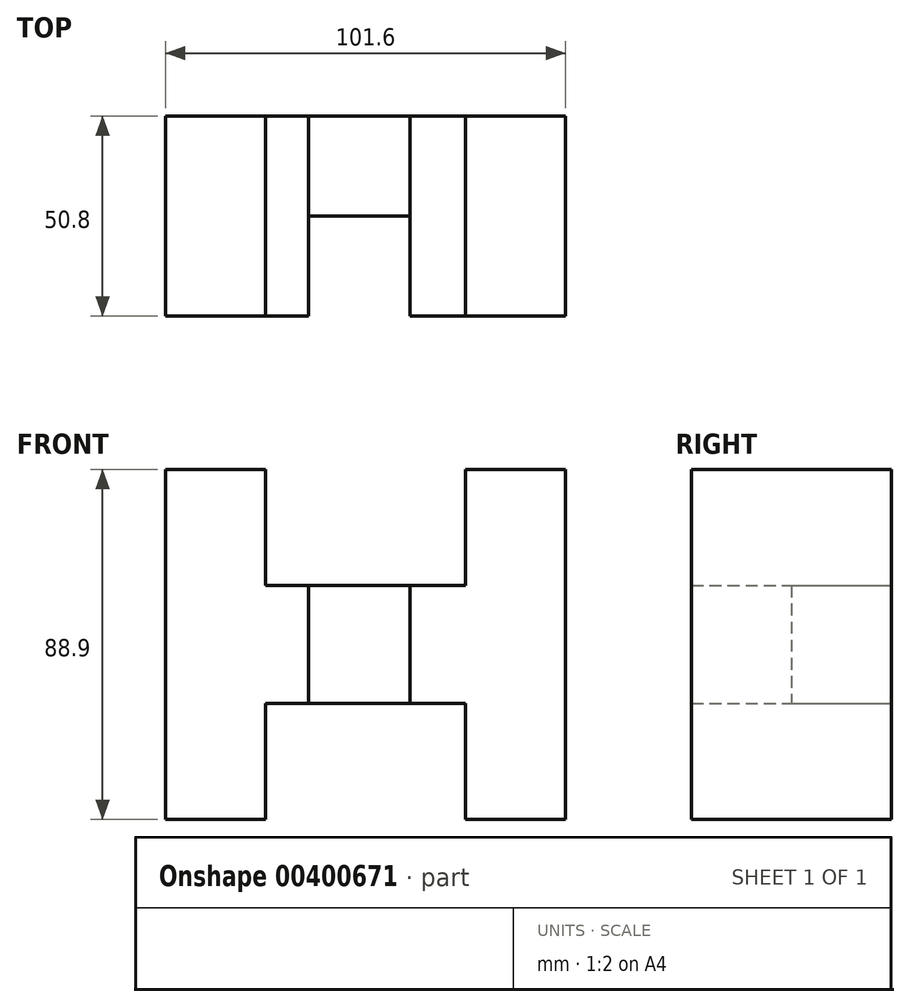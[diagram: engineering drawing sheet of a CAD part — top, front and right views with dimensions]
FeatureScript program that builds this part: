
annotation { "Feature Type Name" : "Feature", "Feature Type Description" : "" }
export const myFeature = defineFeature(function(context is Context, id is Id, definition is map)
    precondition{}
    {
        {
            var Q0;
            Q0=qCreatedBy(makeId("Front.planeOp"),FACE);
            var sketch = newSketch(context, id + "F0", { "sketchPlane" : qUnion([Q0])});
            skLineSegment(sketch, "E0", {"start": v(52.34, 49.99) * mm, "end": v(52.34, -38.91) * mm});
            skLineSegment(sketch, "E1", {"start": v(52.34, -38.91) * mm, "end": v(26.94, -38.91) * mm});
            skLineSegment(sketch, "E2", {"start": v(26.94, -38.91) * mm, "end": v(26.94, -9.45) * mm});
            skLineSegment(sketch, "E3", {"start": v(26.94, -9.45) * mm, "end": v(-23.86, -9.45) * mm});
            skLineSegment(sketch, "E4", {"start": v(-23.86, -9.45) * mm, "end": v(-23.86, -38.91) * mm});
            skLineSegment(sketch, "E5", {"start": v(-23.86, -38.91) * mm, "end": v(-49.26, -38.91) * mm});
            skLineSegment(sketch, "E6", {"start": v(-49.26, -38.91) * mm, "end": v(-49.26, 49.99) * mm});
            skLineSegment(sketch, "E7", {"start": v(-49.26, 49.99) * mm, "end": v(-23.86, 49.99) * mm});
            skLineSegment(sketch, "E8", {"start": v(-23.86, 49.99) * mm, "end": v(-23.86, 20.52) * mm});
            skLineSegment(sketch, "E9", {"start": v(-23.86, 20.52) * mm, "end": v(26.94, 20.52) * mm});
            skLineSegment(sketch, "E10", {"start": v(26.94, 20.52) * mm, "end": v(26.94, 49.99) * mm});
            skLineSegment(sketch, "E11", {"start": v(26.94, 49.99) * mm, "end": v(52.34, 49.99) * mm});
            skLineSegment(sketch, "E12", {"start": v(-12.95, -9.45) * mm, "end": v(-12.95, 20.52) * mm});
            skLineSegment(sketch, "E13", {"start": v(12.88, 0) * mm, "end": v(12.88, 20.52) * mm});
            skLineSegment(sketch, "E14", {"start": v(12.88, 0) * mm, "end": v(12.88, -9.45) * mm});
            skSolve(sketch);
        }
        {
            var Q0;
            {var subQ0=sQuery(id+"F0.wireOp",EDGE,"E4");Q0=makeQuery(id+"F0.imprint","IMPRINT",FACE,{"disambiguationData":[TD([[makeQuery(id+"F0.imprint","IMPRINT",EDGE,{"derivedFrom":subQ0}),-1.0]])]});}
            var Q1;
            Q1=makeQuery(id+"F0.imprint","IMPRINT",FACE,{"disambiguationData":[TD([[makeQuery(id+"F0.imprint","IMPRINT",EDGE,{"derivedFrom":sQuery(id+"F0.wireOp",EDGE,"E0")}),-1.0]])]});
            extrude(context, id + "F1", {"entities" : qUnion([Q0, Q1]), "depth" : 50.8 * mm});
        }
        {
            var Q0;
            {var subQ0=sQuery(id+"F0.wireOp",EDGE,"E12");Q0=makeQuery(id+"F0.imprint","IMPRINT",FACE,{"disambiguationData":[TD([[makeQuery(id+"F0.imprint","IMPRINT",EDGE,{"derivedFrom":subQ0}),-1.0]])]});}
            extrude(context, id + "F2", {"entities" : qUnion([Q0]), "depth" : 25.4 * mm});
        }
    });
